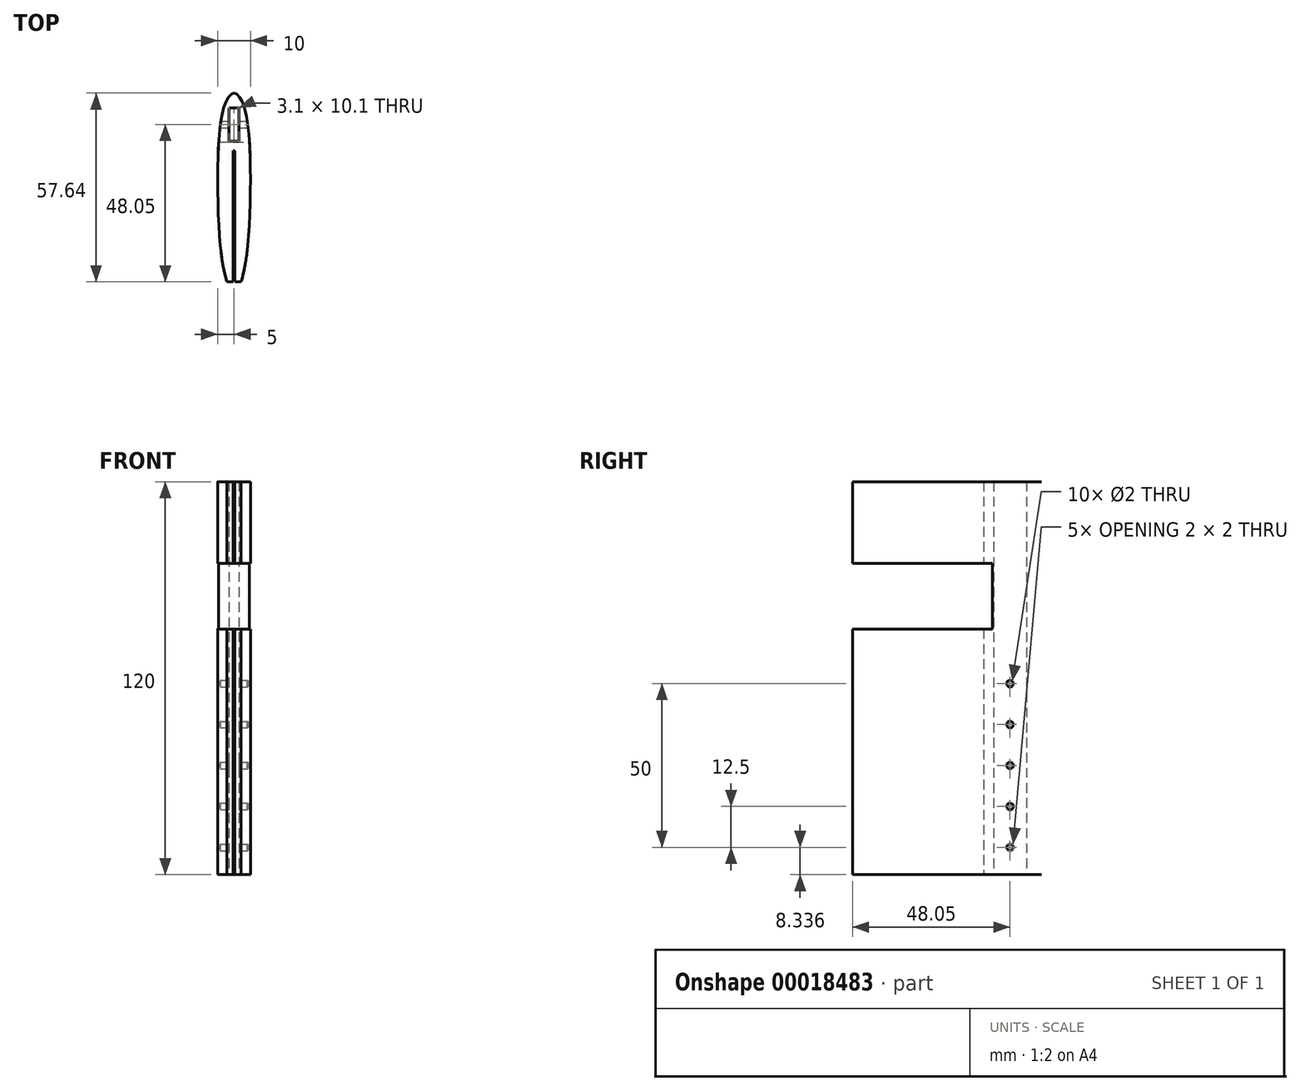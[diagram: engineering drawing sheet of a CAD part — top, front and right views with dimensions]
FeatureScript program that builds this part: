
annotation { "Feature Type Name" : "Feature", "Feature Type Description" : "" }
export const myFeature = defineFeature(function(context is Context, id is Id, definition is map)
    precondition{}
    {
        {
            var Q0;
            Q0=qCreatedBy(makeId("Top.planeOp"),FACE);
            var sketch = newSketch(context, id + "F0", { "sketchPlane" : qUnion([Q0])});
            skLineSegment(sketch, "E0", {"start": v(0, 90) * mm, "end": v(5, 90) * mm});
            skLineSegment(sketch, "E1", {"start": v(5, 90) * mm, "end": v(5, 10) * mm});
            skLineSegment(sketch, "E2", {"start": v(5, 10) * mm, "end": v(90, 10) * mm});
            skLineSegment(sketch, "E3", {"start": v(90, 10) * mm, "end": v(90, 0) * mm});
            skLineSegment(sketch, "E4", {"start": v(90, 0) * mm, "end": v(0, 0) * mm});
            skLineSegment(sketch, "E5.MirrorCS", {"start": v(0, 90) * mm, "end": v(-5, 90) * mm});
            skLineSegment(sketch, "E6.MirrorCS", {"start": v(-5, 90) * mm, "end": v(-5, 10) * mm});
            skLineSegment(sketch, "E7.MirrorCS", {"start": v(-5, 10) * mm, "end": v(-90, 10) * mm});
            skLineSegment(sketch, "E8.MirrorCS", {"start": v(-90, 10) * mm, "end": v(-90, 0) * mm});
            skLineSegment(sketch, "E9.MirrorCS", {"start": v(-90, 0) * mm, "end": v(0, 0) * mm});
            skSolve(sketch);
        }
        {
            var Q0;
            Q0=makeQuery(id+"F0.imprint","IMPRINT",FACE,{"disambiguationData":[TD([[makeQuery(id+"F0.imprint","IMPRINT",EDGE,{"derivedFrom":sQuery(id+"F0.wireOp",EDGE,"E0")}),-1.0]])]});
            extrude(context, id + "F1", {"entities" : qUnion([Q0]), "depth" : 10 * mm});
        }
        {
            var Q0;
            Q0=makeQuery(id+"F1.opExtrude","CAP_FACE",FACE,{"disambiguationData":[OSD([sQuery(id+"F0.wireOp",EDGE,"E0"),sQuery(id+"F0.wireOp",EDGE,"E1"),sQuery(id+"F0.wireOp",EDGE,"E2"),sQuery(id+"F0.wireOp",EDGE,"E3"),sQuery(id+"F0.wireOp",EDGE,"E4"),sQuery(id+"F0.wireOp",EDGE,"E5.MirrorCS"),sQuery(id+"F0.wireOp",EDGE,"E6.MirrorCS"),sQuery(id+"F0.wireOp",EDGE,"E7.MirrorCS"),sQuery(id+"F0.wireOp",EDGE,"E8.MirrorCS"),sQuery(id+"F0.wireOp",EDGE,"E9.MirrorCS")])],"isStart":false});
            var sketch = newSketch(context, id + "F2", { "sketchPlane" : qUnion([Q0])});
            skLineSegment(sketch, "E10.bottom", {"start": v(-5, 80) * mm, "end": v(5, 80) * mm});
            skLineSegment(sketch, "E10.top", {"start": v(-5, 70) * mm, "end": v(5, 70) * mm});
            skLineSegment(sketch, "E10.left", {"start": v(-5, 80) * mm, "end": v(-5, 70) * mm});
            skLineSegment(sketch, "E10.right", {"start": v(5, 80) * mm, "end": v(5, 70) * mm});
            skSolve(sketch);
        }
        {
            var Q0;
            Q0=makeQuery(id+"F2.imprint","IMPRINT",FACE,{"disambiguationData":[TD([[makeQuery(id+"F2.imprint","IMPRINT",EDGE,{"derivedFrom":sQuery(id+"F2.wireOp",EDGE,"E10.bottom")}),-1.0]])]});
            extrude(context, id + "F3", {"entities" : qUnion([Q0]), "operationType" : NewBodyOperationType.ADD, "depth" : 10 * mm});
        }
        {
            var Q0;
            {var subQ0=sQuery(id+"F0.wireOp",EDGE,"E1");var subQ1=sQuery(id+"F0.wireOp",EDGE,"E2");var subQ2=sQuery(id+"F0.wireOp",EDGE,"E3");var subQ3=sQuery(id+"F0.wireOp",EDGE,"E4");var subQ4=sQuery(id+"F0.wireOp",EDGE,"E6.MirrorCS");var subQ5=sQuery(id+"F0.wireOp",EDGE,"E7.MirrorCS");var subQ6=sQuery(id+"F0.wireOp",EDGE,"E8.MirrorCS");var subQ7=sQuery(id+"F0.wireOp",EDGE,"E9.MirrorCS");Q0=makeQuery(id+"F3.boolean.opBoolean","SPLIT",FACE,{"disambiguationData":[TD([makeQuery(id+"F1.opExtrude","SWEPT_FACE",FACE,{"disambiguationData":[OSD([subQ1])]})])],"derivedFrom":makeQuery(id+"F1.opExtrude","CAP_FACE",FACE,{"disambiguationData":[OSD([sQuery(id+"F0.wireOp",EDGE,"E0"),subQ0,subQ1,subQ2,subQ3,sQuery(id+"F0.wireOp",EDGE,"E5.MirrorCS"),subQ4,subQ5,subQ6,subQ7])],"isStart":false})});}
            var sketch = newSketch(context, id + "F4", { "sketchPlane" : qUnion([Q0])});
            skFitSpline(sketch, "E11", {"points": [v(0, 57.64) * mm, v(2.65, 54.58) * mm, v(5, 31.49) * mm, v(3.55, 6.02) * mm, v(2.2, 0) * mm], "startDerivative": vector(17.44, -0.09) * mm, "endDerivative": vector(-5.28, -21) * mm});
            skLineSegment(sketch, "E12", {"start": v(0, 57.64) * mm, "end": v(0, 24.79) * mm, "construction": true});
            skLineSegment(sketch, "E13", {"start": v(2.2, 0) * mm, "end": v(0.25, 0) * mm});
            skLineSegment(sketch, "E14", {"start": v(0.25, 0) * mm, "end": v(0.25, 40) * mm});
            skLineSegment(sketch, "E15", {"start": v(0.25, 40) * mm, "end": v(0, 40) * mm});
            skFitSpline(sketch, "E16.MirrorCS", {"points": [v(0, 57.64) * mm, v(-2.65, 54.58) * mm, v(-5, 31.49) * mm, v(-3.55, 6.02) * mm, v(-2.2, 0) * mm], "startDerivative": vector(-17.44, -0.09) * mm, "endDerivative": vector(5.28, -21) * mm});
            skLineSegment(sketch, "E17.MirrorCS", {"start": v(-0.25, 40) * mm, "end": v(0, 40) * mm});
            skLineSegment(sketch, "E18.MirrorCS", {"start": v(-0.25, 0) * mm, "end": v(-0.25, 40) * mm});
            skLineSegment(sketch, "E19.MirrorCS", {"start": v(-2.2, 0) * mm, "end": v(-0.25, 0) * mm});
            skLineSegment(sketch, "E20.rect.bottom", {"start": v(1.55, 43) * mm, "end": v(-1.55, 43) * mm});
            skLineSegment(sketch, "E20.rect.top", {"start": v(1.55, 53.1) * mm, "end": v(-1.55, 53.1) * mm});
            skLineSegment(sketch, "E20.rect.left", {"start": v(1.55, 43) * mm, "end": v(1.55, 53.1) * mm});
            skLineSegment(sketch, "E20.rect.right", {"start": v(-1.55, 43) * mm, "end": v(-1.55, 53.1) * mm});
            skPoint(sketch, "E20.rect.middle", {"position": v(0, 48.05) * mm});
            skSolve(sketch);
        }
        {
            var Q0;
            {var subQ19=sQuery(id+"F4.wireOp",EDGE,"E13");Q0=makeQuery(id+"F4.imprint","IMPRINT",FACE,{"disambiguationData":[TD([[makeQuery(id+"F4.imprint","IMPRINT",EDGE,{"derivedFrom":subQ19}),1.0]])]});}
            extrude(context, id + "F5", {"entities" : qUnion([Q0]), "operationType" : NewBodyOperationType.ADD, "depth" : 130 * mm});
        }
        {
            var Q0;
            Q0=qCreatedBy(makeId("Right.planeOp"),FACE);
            var sketch = newSketch(context, id + "F6", { "sketchPlane" : qUnion([Q0])});
            skLineSegment(sketch, "E21.bottom", {"start": v(-13.73, 95) * mm, "end": v(42.64, 95) * mm});
            skLineSegment(sketch, "E21.top", {"start": v(-13.73, 115) * mm, "end": v(42.64, 115) * mm});
            skLineSegment(sketch, "E21.left", {"start": v(-13.73, 95) * mm, "end": v(-13.73, 115) * mm});
            skLineSegment(sketch, "E21.right", {"start": v(42.64, 95) * mm, "end": v(42.64, 115) * mm});
            skSolve(sketch);
        }
        {
            var Q0;
            Q0=makeQuery(id+"F6.imprint","IMPRINT",FACE,{"disambiguationData":[TD([[makeQuery(id+"F6.imprint","IMPRINT",EDGE,{"derivedFrom":sQuery(id+"F6.wireOp",EDGE,"E21.bottom")}),1.0]])]});
            extrude(context, id + "F7", {"entities" : qUnion([Q0]), "operationType" : NewBodyOperationType.REMOVE, "endBound" : BoundingType.THROUGH_ALL, "oppositeDirection" : true, "depth" : 25 * mm, "hasSecondDirection" : true, "secondDirectionBound" : SecondDirectionBoundingType.THROUGH_ALL, "secondDirectionOppositeDirection" : false, "secondDirectionDepth" : 25 * mm});
        }
        {
            var Q0;
            Q0=qCreatedBy(makeId("Top.planeOp"),FACE);
            var sketch = newSketch(context, id + "F8", { "sketchPlane" : qUnion([Q0])});
            skLineSegment(sketch, "E22.rect.bottom", {"start": v(115.77, -104.9) * mm, "end": v(-115.77, -104.9) * mm});
            skLineSegment(sketch, "E22.rect.top", {"start": v(115.77, 104.9) * mm, "end": v(-115.77, 104.9) * mm});
            skLineSegment(sketch, "E22.rect.left", {"start": v(115.77, -104.9) * mm, "end": v(115.77, 104.9) * mm});
            skLineSegment(sketch, "E22.rect.right", {"start": v(-115.77, -104.9) * mm, "end": v(-115.77, 104.9) * mm});
            skPoint(sketch, "E22.rect.middle", {"position": v(0, 0) * mm});
            skSolve(sketch);
        }
        {
            var Q0;
            Q0 = qSketchRegion(id + "F8", true);
            var Q1;
            Q1=makeQuery(id+"F3.opExtrude","CAP_FACE",FACE,{"disambiguationData":[OSD([sQuery(id+"F2.wireOp",EDGE,"E10.bottom"),sQuery(id+"F2.wireOp",EDGE,"E10.top"),sQuery(id+"F2.wireOp",EDGE,"E10.left"),sQuery(id+"F2.wireOp",EDGE,"E10.right")])],"isStart":false});
            extrude(context, id + "F9", {"entities" : qUnion([Q0]), "operationType" : NewBodyOperationType.REMOVE, "endBound" : BoundingType.UP_TO_SURFACE, "endBoundEntityFace" : qUnion([Q1]), "depth" : 25 * mm});
        }
        {
            var Q0;
            Q0=qCreatedBy(makeId("Right.planeOp"),FACE);
            var sketch = newSketch(context, id + "F10", { "sketchPlane" : qUnion([Q0])});
            skCircle(sketch, "E23", {"center": v(48.05, 28.34) * mm, "radius": 1 * mm});
            skCircle(sketch, "E24.1.0.0", {"center": v(48.05, 40.84) * mm, "radius": 1 * mm});
            skCircle(sketch, "E24.2.0.0", {"center": v(48.05, 53.34) * mm, "radius": 1 * mm});
            skLineSegment(sketch, "E24.direction1", {"start": v(48.05, 28.34) * mm, "end": v(48.05, 40.84) * mm, "construction": true});
            skCircle(sketch, "E25.0.3.0", {"center": v(48.05, 65.84) * mm, "radius": 1 * mm});
            skCircle(sketch, "E25.0.4.0", {"center": v(48.05, 78.34) * mm, "radius": 1 * mm});
            skSolve(sketch);
        }
        {
            var Q0;
            Q0 = qSketchRegion(id + "F10", true);
            extrude(context, id + "F11", {"entities" : qUnion([Q0]), "operationType" : NewBodyOperationType.REMOVE, "endBound" : BoundingType.THROUGH_ALL, "oppositeDirection" : true, "depth" : 25 * mm, "hasSecondDirection" : true, "secondDirectionBound" : SecondDirectionBoundingType.THROUGH_ALL, "secondDirectionOppositeDirection" : false, "secondDirectionDepth" : 25 * mm});
        }
    });
